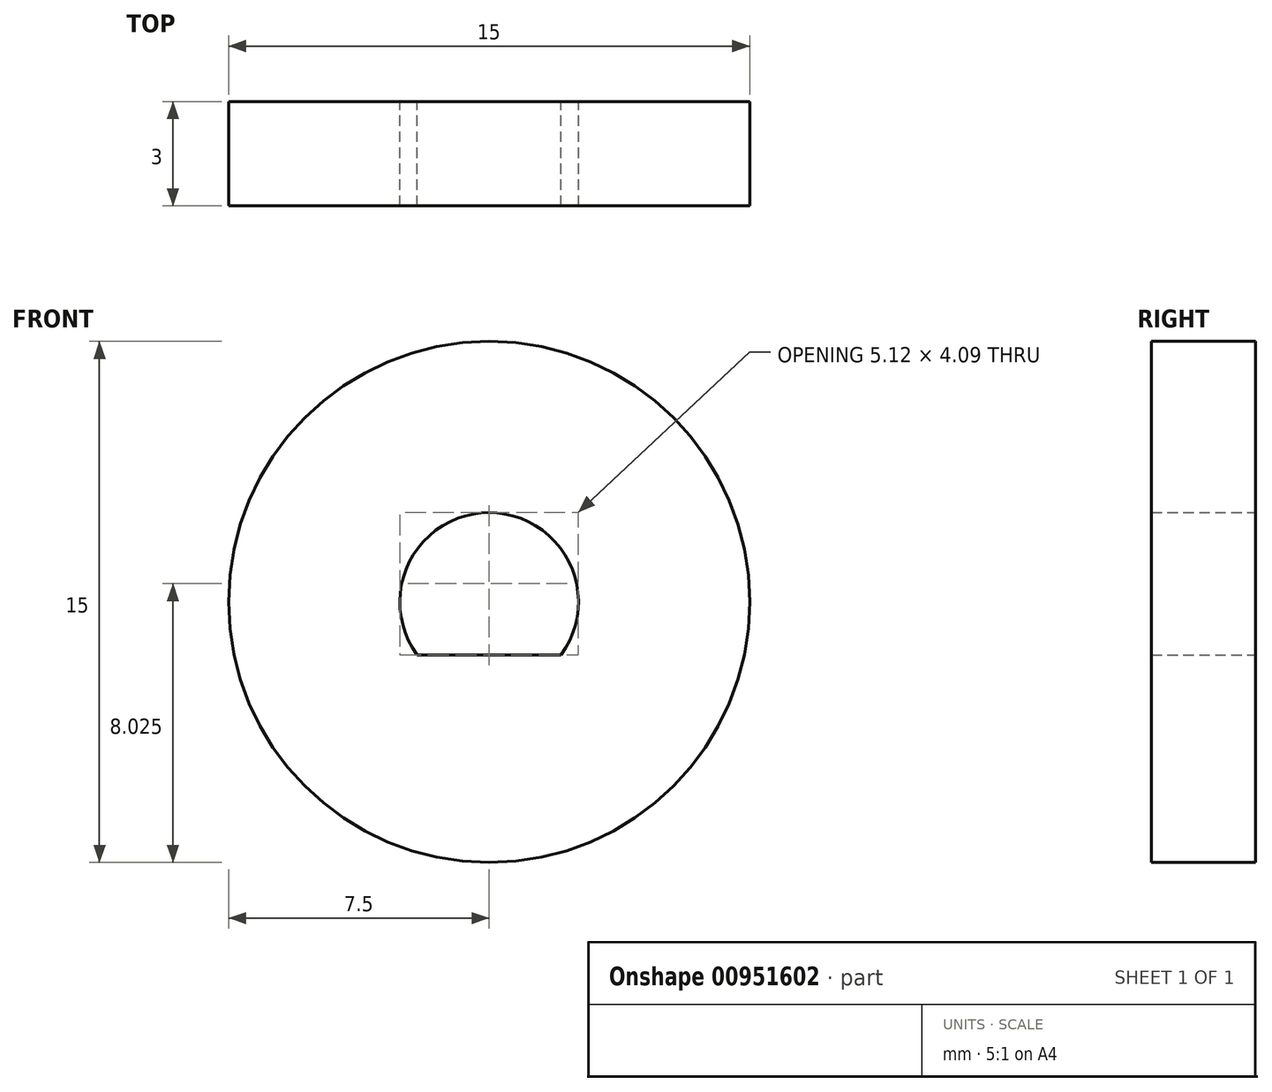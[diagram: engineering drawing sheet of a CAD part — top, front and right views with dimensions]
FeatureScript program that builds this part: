
annotation { "Feature Type Name" : "Feature", "Feature Type Description" : "" }
export const myFeature = defineFeature(function(context is Context, id is Id, definition is map)
    precondition{}
    {
        {
            var Q0;
            Q0=qCreatedBy(makeId("Front.planeOp"),FACE);
            var sketch = newSketch(context, id + "F0", { "sketchPlane" : qUnion([Q0])});
            skCircle(sketch, "E0", {"center": v(0, 0) * mm, "radius": 7.5 * mm});
            skLineSegment(sketch, "E1", {"start": v(0, 2.57) * mm, "end": v(0, -1.52) * mm, "construction": true});
            skLineSegment(sketch, "E2", {"start": v(0, -1.52) * mm, "end": v(2.07, -1.52) * mm});
            skLineSegment(sketch, "E3.MirrorCS", {"start": v(0, -1.52) * mm, "end": v(-2.07, -1.52) * mm});
            skArc(sketch, "E4", {"start": v(2.07, -1.52) * mm, "mid": v(0, 2.57) * mm, "end": v(-2.07, -1.52) * mm});
            skSolve(sketch);
        }
        {
            var Q0;
            Q0=qSketchRegion(id+"F0",true);
            extrude(context, id + "F1", {"entities" : qUnion([Q0]), "depth" : 3 * mm, "offsetDistance" : 25 * mm});
        }
    });
